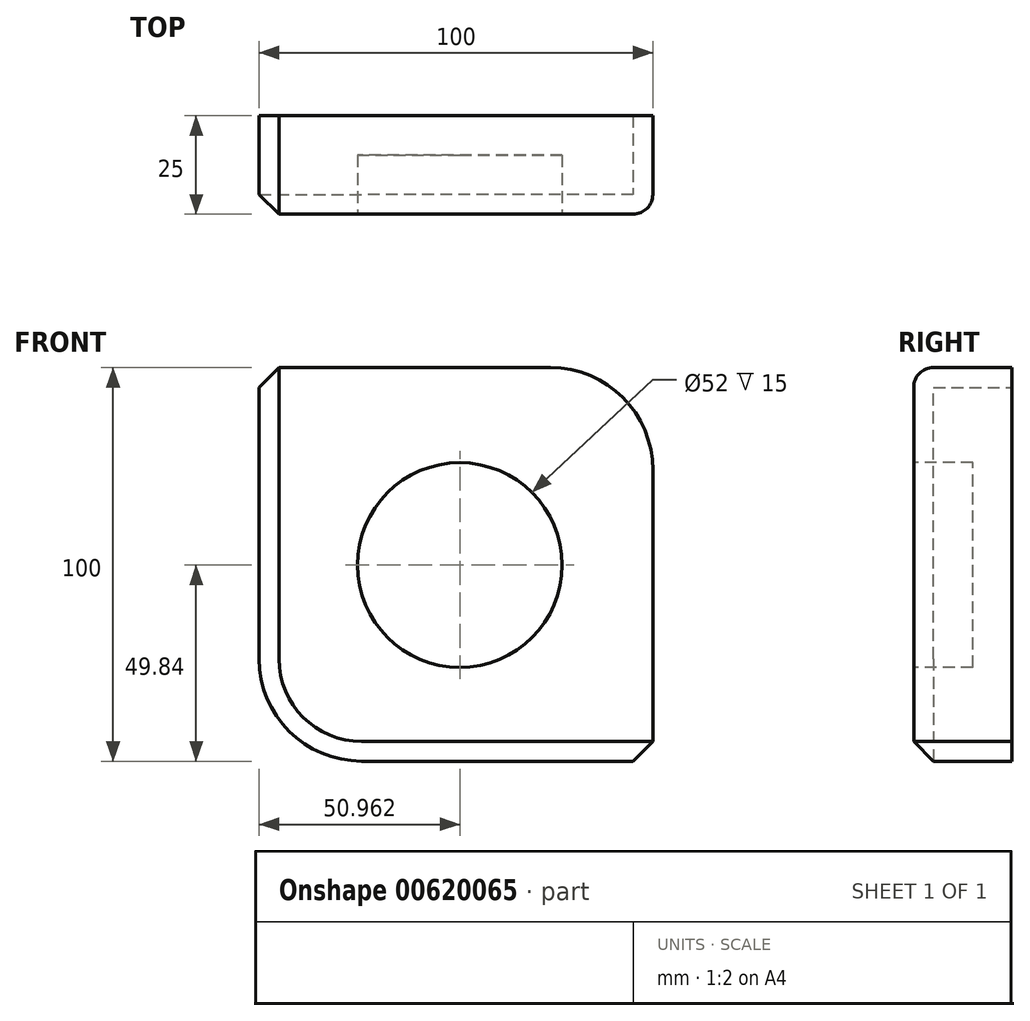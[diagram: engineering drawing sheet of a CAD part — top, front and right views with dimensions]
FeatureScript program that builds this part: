
annotation { "Feature Type Name" : "Feature", "Feature Type Description" : "" }
export const myFeature = defineFeature(function(context is Context, id is Id, definition is map)
    precondition{}
    {
        {
            var Q0;
            Q0=qCreatedBy(makeId("Front.planeOp"),FACE);
            var sketch = newSketch(context, id + "F0", { "sketchPlane" : qUnion([Q0])});
            skLineSegment(sketch, "E0.bottom", {"start": v(-43.5, 50.16) * mm, "end": v(30.5, 50.16) * mm});
            skLineSegment(sketch, "E0.top", {"start": v(-17.5, -49.84) * mm, "end": v(56.5, -49.84) * mm});
            skLineSegment(sketch, "E0.left", {"start": v(-43.5, 50.16) * mm, "end": v(-43.5, -23.84) * mm});
            skLineSegment(sketch, "E0.right", {"start": v(56.5, 24.16) * mm, "end": v(56.5, -49.84) * mm});
            skPoint(sketch, "E1.visualSharp", {"position": v(56.5, 50.16) * mm});
            skArc(sketch, "E1.filletArc", {"start": v(56.5, 24.16) * mm, "mid": v(48.9, 42.55) * mm, "end": v(30.5, 50.16) * mm});
            skPoint(sketch, "E2.visualSharp", {"position": v(-43.5, -49.84) * mm});
            skArc(sketch, "E2.filletArc", {"start": v(-43.5, -23.84) * mm, "mid": v(-35.88, -42.22) * mm, "end": v(-17.5, -49.84) * mm});
            skSolve(sketch);
        }
        {
            var Q0;
            Q0=makeQuery(id+"F0.imprint","IMPRINT",FACE,{"disambiguationData":[TD([[makeQuery(id+"F0.imprint","IMPRINT",EDGE,{"derivedFrom":sQuery(id+"F0.wireOp",EDGE,"E0.bottom")}),-1.0]])]});
            extrude(context, id + "F1", {"entities" : qUnion([Q0]), "depth" : 25 * mm, "offsetDistance" : 25 * mm});
        }
        {
            var Q0;
            Q0=makeQuery(id+"F1.opExtrude","CAP_EDGE",EDGE,{"disambiguationData":[OSD([sQuery(id+"F0.wireOp",EDGE,"E0.bottom")])],"isStart":false});
            fillet(context, id + "F2", {"entities" : qUnion([Q0]), "radius" : 5 * mm, "tangentPropagation" : true, "allowEdgeOverflow" : false});
        }
        {
            var Q0;
            Q0=makeQuery(id+"F1.opExtrude","SWEPT_EDGE",EDGE,{"disambiguationData":[OSD([sQuery(id+"F0.wireOp",EDGE,"E0.bottom"),sQuery(id+"F0.wireOp",EDGE,"E0.left")])]});
            chamfer(context, id + "F3", {"entities" : qUnion([Q0]), "width" : 5 * mm, "tangentPropagation" : true});
        }
        {
            var Q0;
            Q0=makeQuery(id+"F1.opExtrude","CAP_FACE",FACE,{"disambiguationData":[OSD([sQuery(id+"F0.wireOp",EDGE,"E0.bottom"),sQuery(id+"F0.wireOp",EDGE,"E0.top"),sQuery(id+"F0.wireOp",EDGE,"E0.left"),sQuery(id+"F0.wireOp",EDGE,"E0.right"),sQuery(id+"F0.wireOp",EDGE,"E1.filletArc"),sQuery(id+"F0.wireOp",EDGE,"E2.filletArc")])],"isStart":false});
            var sketch = newSketch(context, id + "F4", { "sketchPlane" : qUnion([Q0])});
            skCircle(sketch, "E3", {"center": v(7.47, 0) * mm, "radius": 26 * mm});
            skSolve(sketch);
        }
        {
            var Q0;
            Q0=makeQuery(id+"F4.imprint","IMPRINT",FACE,{"disambiguationData":[TD([[makeQuery(id+"F4.imprint","IMPRINT",EDGE,{"derivedFrom":sQuery(id+"F4.wireOp",EDGE,"E3")}),1.0]])]});
            extrude(context, id + "F5", {"entities" : qUnion([Q0]), "operationType" : NewBodyOperationType.REMOVE, "oppositeDirection" : true, "depth" : 15 * mm, "offsetDistance" : 25 * mm});
        }
    });
